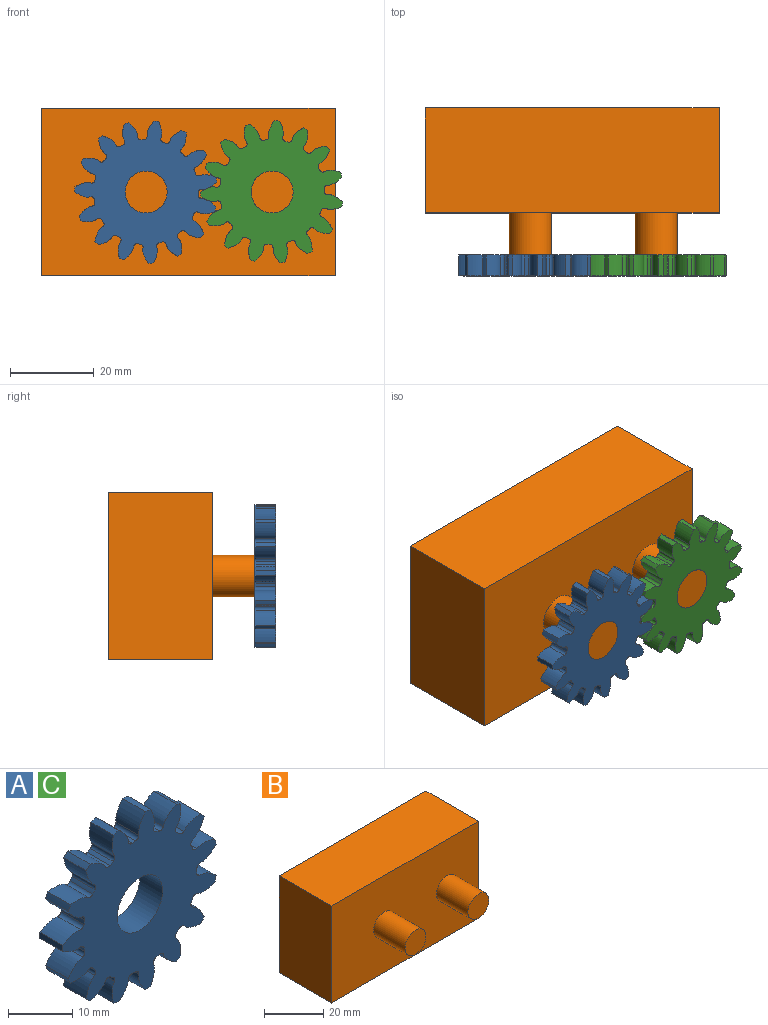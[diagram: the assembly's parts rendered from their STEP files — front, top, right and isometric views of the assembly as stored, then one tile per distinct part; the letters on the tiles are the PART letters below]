
ASSEMBLY  parts=3 mates=2
PART A: 93 faces, bbox 33.8x5x34 mm
  f0: extruded ~5x3.6mm, area 20.9mm2, adj f60,f61,f62,f63
  f1: cylinder r=12.5mm len=5mm, axis (0,1,0), area 3.9mm2, adj f61,f62,f63,f64
  f2: extruded ~5x3.6mm, area 20.9mm2, adj f3,f61,f62,f64
  f3: cylinder r=17mm len=5mm, axis (0,1,0), area 5.9mm2, adj f2,f4,f61,f62
  f4: extruded ~5x4.04mm, area 20.9mm2, adj f3,f61,f62,f65
  f5: cylinder r=12.5mm len=5mm, axis (0,1,0), area 3.9mm2, adj f61,f62,f65,f66
  f6: extruded ~5x3.15mm, area 20.9mm2, adj f7,f61,f62,f66
  f7: cylinder r=17mm len=5mm, axis (0,1,0), area 5.9mm2, adj f6,f8,f61,f62
  f8: extruded ~5x3.78mm, area 20.9mm2, adj f7,f61,f62,f67
  f9: cylinder r=12.5mm len=5mm, axis (0,1,0), area 3.9mm2, adj f61,f62,f67,f68
  f10: extruded ~5x3.91mm, area 20.9mm2, adj f11,f61,f62,f68
  f11: cylinder r=17mm len=5mm, axis (0,1,0), area 5.9mm2, adj f10,f12,f61,f62
  f12: extruded ~5x2.87mm, area 20.9mm2, adj f11,f61,f62,f69
  f13: cylinder r=12.5mm len=5mm, axis (0,1,0), area 3.9mm2, adj f61,f62,f69,f70
  f14: extruded ~5x3.99mm, area 20.9mm2, adj f15,f61,f62,f70
  f15: cylinder r=17mm len=5mm, axis (0,1,0), area 5.9mm2, adj f14,f16,f61,f62
  f16: extruded ~5x3.77mm, area 20.9mm2, adj f15,f61,f62,f71
  f17: cylinder r=12.5mm len=5mm, axis (0,1,0), area 3.9mm2, adj f61,f62,f71,f72
  f18: extruded ~5x3.39mm, area 20.9mm2, adj f19,f61,f62,f72
  f19: cylinder r=17mm len=5mm, axis (0,1,0), area 5.9mm2, adj f18,f20,f61,f62
  f20: extruded ~5x4.04mm, area 20.9mm2, adj f19,f61,f62,f73
  f21: cylinder r=12.5mm len=5mm, axis (0,1,0), area 3.9mm2, adj f61,f62,f73,f74
  f22: extruded ~5x3.4mm, area 20.9mm2, adj f23,f61,f62,f74
  f23: cylinder r=17mm len=5mm, axis (0,1,0), area 5.9mm2, adj f22,f24,f61,f62
  f24: extruded ~5x3.61mm, area 20.9mm2, adj f23,f61,f62,f75
  f25: cylinder r=12.5mm len=5mm, axis (0,1,0), area 3.9mm2, adj f61,f62,f75,f76
  f26: extruded ~5x4mm, area 20.9mm2, adj f27,f61,f62,f76
  f27: cylinder r=17mm len=5mm, axis (0,1,0), area 5.9mm2, adj f26,f28,f61,f62
  f28: extruded ~5x3.14mm, area 20.9mm2, adj f27,f61,f62,f77
  f29: cylinder r=12.5mm len=5mm, axis (0,1,0), area 3.9mm2, adj f61,f62,f77,f78
  f30: extruded ~5x3.91mm, area 20.9mm2, adj f31,f61,f62,f78
  f31: cylinder r=17mm len=5mm, axis (0,1,0), area 5.9mm2, adj f30,f32,f61,f62
  f32: extruded ~5x3.91mm, area 20.9mm2, adj f31,f61,f62,f79
  f33: cylinder r=12.5mm len=5mm, axis (0,1,0), area 3.9mm2, adj f61,f62,f79,f80
  f34: extruded ~5x3.14mm, area 20.9mm2, adj f35,f61,f62,f80
  f35: cylinder r=17mm len=5mm, axis (0,1,0), area 5.9mm2, adj f34,f36,f61,f62
  f36: extruded ~5x4mm, area 20.9mm2, adj f35,f61,f62,f81
  f37: cylinder r=12.5mm len=5mm, axis (0,1,0), area 3.9mm2, adj f61,f62,f81,f82
  f38: extruded ~5x3.61mm, area 20.9mm2, adj f39,f61,f62,f82
  f39: cylinder r=17mm len=5mm, axis (0,1,0), area 5.9mm2, adj f38,f40,f61,f62
  f40: extruded ~5x3.4mm, area 20.9mm2, adj f39,f61,f62,f83
  f41: cylinder r=12.5mm len=5mm, axis (0,1,0), area 3.9mm2, adj f61,f62,f83,f84
  f42: extruded ~5x4.04mm, area 20.9mm2, adj f43,f61,f62,f84
  f43: cylinder r=17mm len=5mm, axis (0,1,0), area 5.9mm2, adj f42,f44,f61,f62
  f44: extruded ~5x3.39mm, area 20.9mm2, adj f43,f61,f62,f85
  f45: cylinder r=12.5mm len=5mm, axis (0,1,0), area 3.9mm2, adj f61,f62,f85,f86
  f46: extruded ~5x3.77mm, area 20.9mm2, adj f47,f61,f62,f86
  f47: cylinder r=17mm len=5mm, axis (0,1,0), area 5.9mm2, adj f46,f48,f61,f62
  f48: extruded ~5x3.99mm, area 20.9mm2, adj f47,f61,f62,f87
  f49: cylinder r=12.5mm len=5mm, axis (0,1,0), area 3.9mm2, adj f61,f62,f87,f88
  f50: extruded ~5x2.87mm, area 20.9mm2, adj f51,f61,f62,f88
  f51: cylinder r=17mm len=5mm, axis (0,1,0), area 5.9mm2, adj f50,f52,f61,f62
  f52: extruded ~5x3.91mm, area 20.9mm2, adj f51,f61,f62,f89
  f53: cylinder r=12.5mm len=5mm, axis (0,1,0), area 3.9mm2, adj f61,f62,f89,f90
  f54: extruded ~5x3.78mm, area 20.9mm2, adj f55,f61,f62,f90
  f55: cylinder r=17mm len=5mm, axis (0,1,0), area 5.9mm2, adj f54,f56,f61,f62
  f56: extruded ~5x3.15mm, area 20.9mm2, adj f55,f61,f62,f91
  f57: cylinder r=12.5mm len=5mm, axis (0,1,0), area 3.9mm2, adj f61,f62,f91,f92
  f58: extruded ~5x4.04mm, area 20.9mm2, adj f60,f61,f62,f92
  f59: cylinder r=5mm len=10mm, axis (0,1,0), area 157.1mm2, adj f61,f62
  f60: cylinder r=17mm len=5mm, axis (0,1,0), area 5.9mm2, adj f0,f58,f61,f62
  f61: plane 33.96x33.78mm, normal (0,-1,0), area 608.5mm2, adj f0,f1,f2,f3,f4,f5,f6,f7
  f62: plane 33.96x33.78mm, normal (0,1,0), area 608.5mm2, adj f0,f1,f2,f3,f4,f5,f6,f7
  f63: cylinder r=0.7mm len=5mm, axis (0,1,0), area 5.4mm2, adj f0,f1,f61,f62
  f64: cylinder r=0.7mm len=5mm, axis (0,1,0), area 5.4mm2, adj f1,f2,f61,f62
  f65: cylinder r=0.7mm len=5mm, axis (0,1,0), area 5.4mm2, adj f4,f5,f61,f62
  f66: cylinder r=0.7mm len=5mm, axis (0,1,0), area 5.4mm2, adj f5,f6,f61,f62
  f67: cylinder r=0.7mm len=5mm, axis (0,1,0), area 5.4mm2, adj f8,f9,f61,f62
  f68: cylinder r=0.7mm len=5mm, axis (0,1,0), area 5.4mm2, adj f9,f10,f61,f62
  f69: cylinder r=0.7mm len=5mm, axis (0,1,0), area 5.4mm2, adj f12,f13,f61,f62
  f70: cylinder r=0.7mm len=5mm, axis (0,1,0), area 5.4mm2, adj f13,f14,f61,f62
  f71: cylinder r=0.7mm len=5mm, axis (0,1,0), area 5.4mm2, adj f16,f17,f61,f62
  f72: cylinder r=0.7mm len=5mm, axis (0,1,0), area 5.4mm2, adj f17,f18,f61,f62
  f73: cylinder r=0.7mm len=5mm, axis (0,1,0), area 5.4mm2, adj f20,f21,f61,f62
  f74: cylinder r=0.7mm len=5mm, axis (0,1,0), area 5.4mm2, adj f21,f22,f61,f62
  f75: cylinder r=0.7mm len=5mm, axis (0,1,0), area 5.4mm2, adj f24,f25,f61,f62
  f76: cylinder r=0.7mm len=5mm, axis (0,1,0), area 5.4mm2, adj f25,f26,f61,f62
  f77: cylinder r=0.7mm len=5mm, axis (0,1,0), area 5.4mm2, adj f28,f29,f61,f62
  f78: cylinder r=0.7mm len=5mm, axis (0,1,0), area 5.4mm2, adj f29,f30,f61,f62
  f79: cylinder r=0.7mm len=5mm, axis (0,1,0), area 5.4mm2, adj f32,f33,f61,f62
  f80: cylinder r=0.7mm len=5mm, axis (0,1,0), area 5.4mm2, adj f33,f34,f61,f62
  f81: cylinder r=0.7mm len=5mm, axis (0,1,0), area 5.4mm2, adj f36,f37,f61,f62
  f82: cylinder r=0.7mm len=5mm, axis (0,1,0), area 5.4mm2, adj f37,f38,f61,f62
  f83: cylinder r=0.7mm len=5mm, axis (0,1,0), area 5.4mm2, adj f40,f41,f61,f62
  f84: cylinder r=0.7mm len=5mm, axis (0,1,0), area 5.4mm2, adj f41,f42,f61,f62
  f85: cylinder r=0.7mm len=5mm, axis (0,1,0), area 5.4mm2, adj f44,f45,f61,f62
  f86: cylinder r=0.7mm len=5mm, axis (0,1,0), area 5.4mm2, adj f45,f46,f61,f62
  f87: cylinder r=0.7mm len=5mm, axis (0,1,0), area 5.4mm2, adj f48,f49,f61,f62
  f88: cylinder r=0.7mm len=5mm, axis (0,1,0), area 5.4mm2, adj f49,f50,f61,f62
  f89: cylinder r=0.7mm len=5mm, axis (0,1,0), area 5.4mm2, adj f52,f53,f61,f62
  f90: cylinder r=0.7mm len=5mm, axis (0,1,0), area 5.4mm2, adj f53,f54,f61,f62
  f91: cylinder r=0.7mm len=5mm, axis (0,1,0), area 5.4mm2, adj f56,f57,f61,f62
  f92: cylinder r=0.7mm len=5mm, axis (0,1,0), area 5.4mm2, adj f57,f58,f61,f62
PART B: 10 faces, bbox 70x40x40 mm
  f0: plane 40x25mm, normal (-1,0,0), area 1000mm2, adj f1,f3,f4,f5
  f1: plane 70x25mm, normal (0,0,-1), area 1750mm2, adj f0,f2,f4,f5
  f2: plane 40x25mm, normal (1,0,0), area 1000mm2, adj f1,f3,f4,f5
  f3: plane 70x25mm, normal (0,0,1), area 1750mm2, adj f0,f2,f4,f5
  f4: plane 70x40mm, normal (0,-1,0), area 2642.9mm2, adj f0,f1,f2,f3,f6,f8
  f5: plane 70x40mm, normal (0,1,0), area 2800mm2, adj f0,f1,f2,f3
  f6: cylinder r=5mm len=15mm, axis (0,1,0), area 471.2mm2, adj f4,f7
  f7: plane 10x10mm, normal (0,-1,0), area 78.5mm2, adj f6
  f8: cylinder r=5mm len=15mm, axis (0,1,0), area 471.2mm2, adj f4,f9
  f9: plane 10x10mm, normal (0,-1,0), area 78.5mm2, adj f8
PART C: same geometry as A
PLACE A rot(axis=(0,-1,0),165.9deg) t=(-28.01,-32.51,-10.67)mm
PLACE B t=(-18.01,2.49,-10.67)mm fixed
PLACE C rot(axis=(0,1,0),165.9deg) t=(1.99,-32.51,-10.67)mm
MATE revolute C.f3 <-> B.f8  axis (0,-1,0) through (1.99,-37.51,-10.67)mm
MATE revolute A.f3 <-> B.f6  axis (0,-1,0) through (-28.01,-37.51,-10.67)mm
